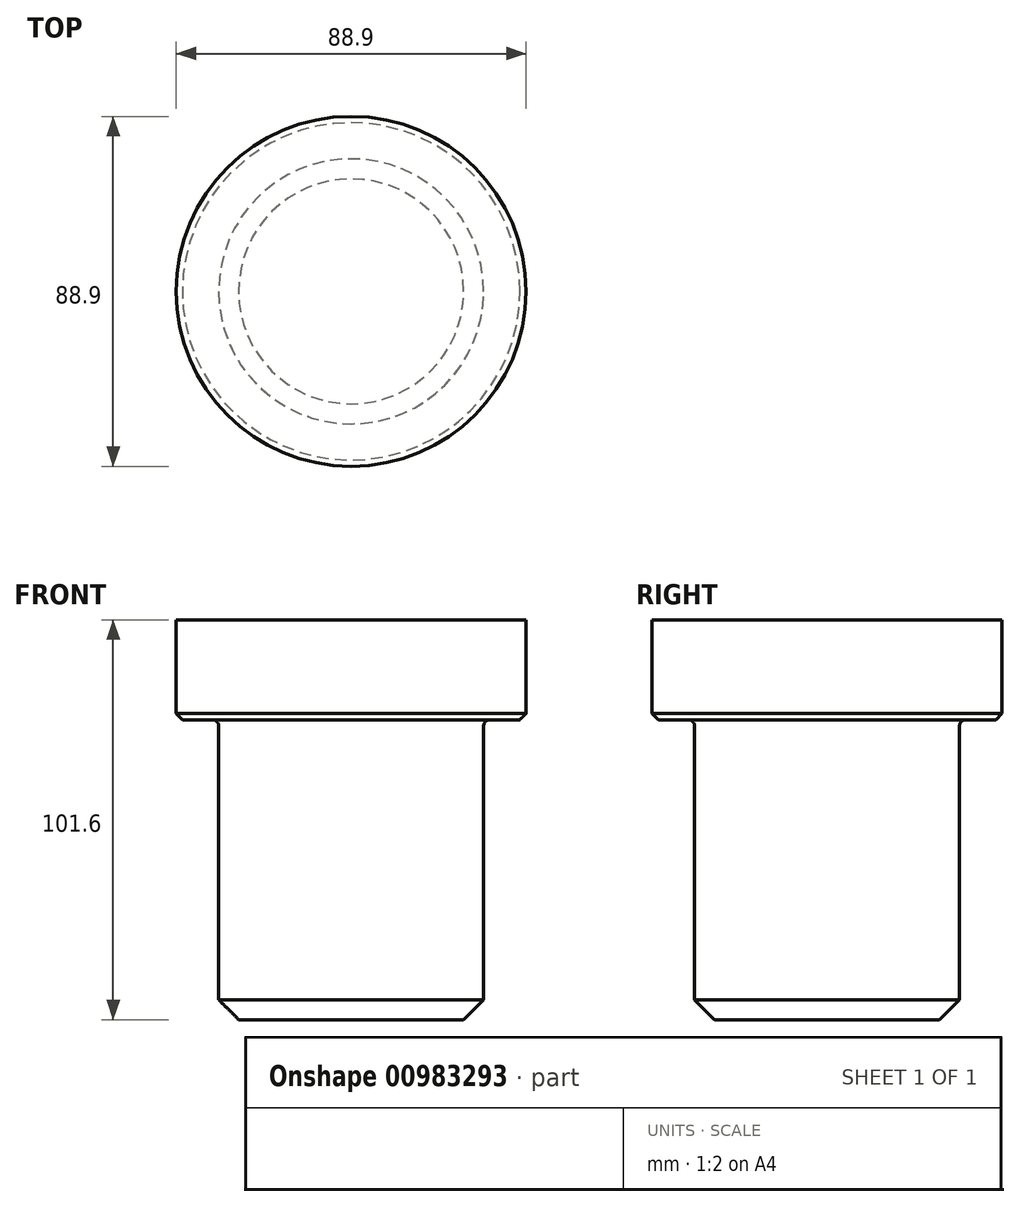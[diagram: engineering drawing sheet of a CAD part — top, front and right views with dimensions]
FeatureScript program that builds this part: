
annotation { "Feature Type Name" : "Feature", "Feature Type Description" : "" }
export const myFeature = defineFeature(function(context is Context, id is Id, definition is map)
    precondition{}
    {
        {
            var Q0;
            Q0=qCreatedBy(makeId("Front.planeOp"),FACE);
            var sketch = newSketch(context, id + "F0", { "sketchPlane" : qUnion([Q0])});
            skLineSegment(sketch, "E0", {"start": v(0, -50.8) * mm, "end": v(0, 50.8) * mm});
            skLineSegment(sketch, "E1", {"start": v(0, 50.8) * mm, "end": v(44.45, 50.8) * mm});
            skLineSegment(sketch, "E2", {"start": v(44.45, 25.4) * mm, "end": v(44.45, 50.8) * mm});
            skLineSegment(sketch, "E3", {"start": v(44.45, 25.4) * mm, "end": v(33.65, 25.4) * mm});
            skLineSegment(sketch, "E4", {"start": v(0, -50.8) * mm, "end": v(33.66, -50.8) * mm});
            skLineSegment(sketch, "E5", {"start": v(33.65, 25.4) * mm, "end": v(33.66, -50.8) * mm});
            skSolve(sketch);
        }
        {
            var Q0;
            Q0=makeQuery(id+"F0.imprint","IMPRINT",FACE,{"disambiguationData":[TD([[makeQuery(id+"F0.imprint","IMPRINT",EDGE,{"derivedFrom":sQuery(id+"F0.wireOp",EDGE,"E0")}),-1.0]])]});
            var Q1;
            Q1=sQuery(id+"F0.wireOp",EDGE,"E0");
            revolve(context, id + "F1", {"surfaceOperationType" : NewSurfaceOperationType.NEW, "entities" : qUnion([Q0]), "axis" : qUnion([Q1]), "revolveType" : RevolveType.FULL});
        }
        {
            var Q0;
            Q0=makeQuery(id+"F1.opRevolve","SWEPT_EDGE",EDGE,{"disambiguationData":[OSD([sQuery(id+"F0.wireOp",EDGE,"E3"),sQuery(id+"F0.wireOp",EDGE,"E5")])]});
            fillet(context, id + "F2", {"entities" : qUnion([Q0]), "radius" : 1.59 * mm, "tangentPropagation" : true, "allowEdgeOverflow" : false});
        }
        {
            var Q0;
            Q0=makeQuery(id+"F1.opRevolve","SWEPT_EDGE",EDGE,{"disambiguationData":[OSD([sQuery(id+"F0.wireOp",EDGE,"E2"),sQuery(id+"F0.wireOp",EDGE,"E3")])]});
            chamfer(context, id + "F3", {"entities" : qUnion([Q0]), "width" : 1.59 * mm, "tangentPropagation" : true});
        }
        {
            var Q0;
            Q0=makeQuery(id+"F1.opRevolve","SWEPT_EDGE",EDGE,{"disambiguationData":[OSD([sQuery(id+"F0.wireOp",EDGE,"E4"),sQuery(id+"F0.wireOp",EDGE,"E5")])]});
            chamfer(context, id + "F4", {"entities" : qUnion([Q0]), "width" : 5.08 * mm, "tangentPropagation" : true});
        }
    });
